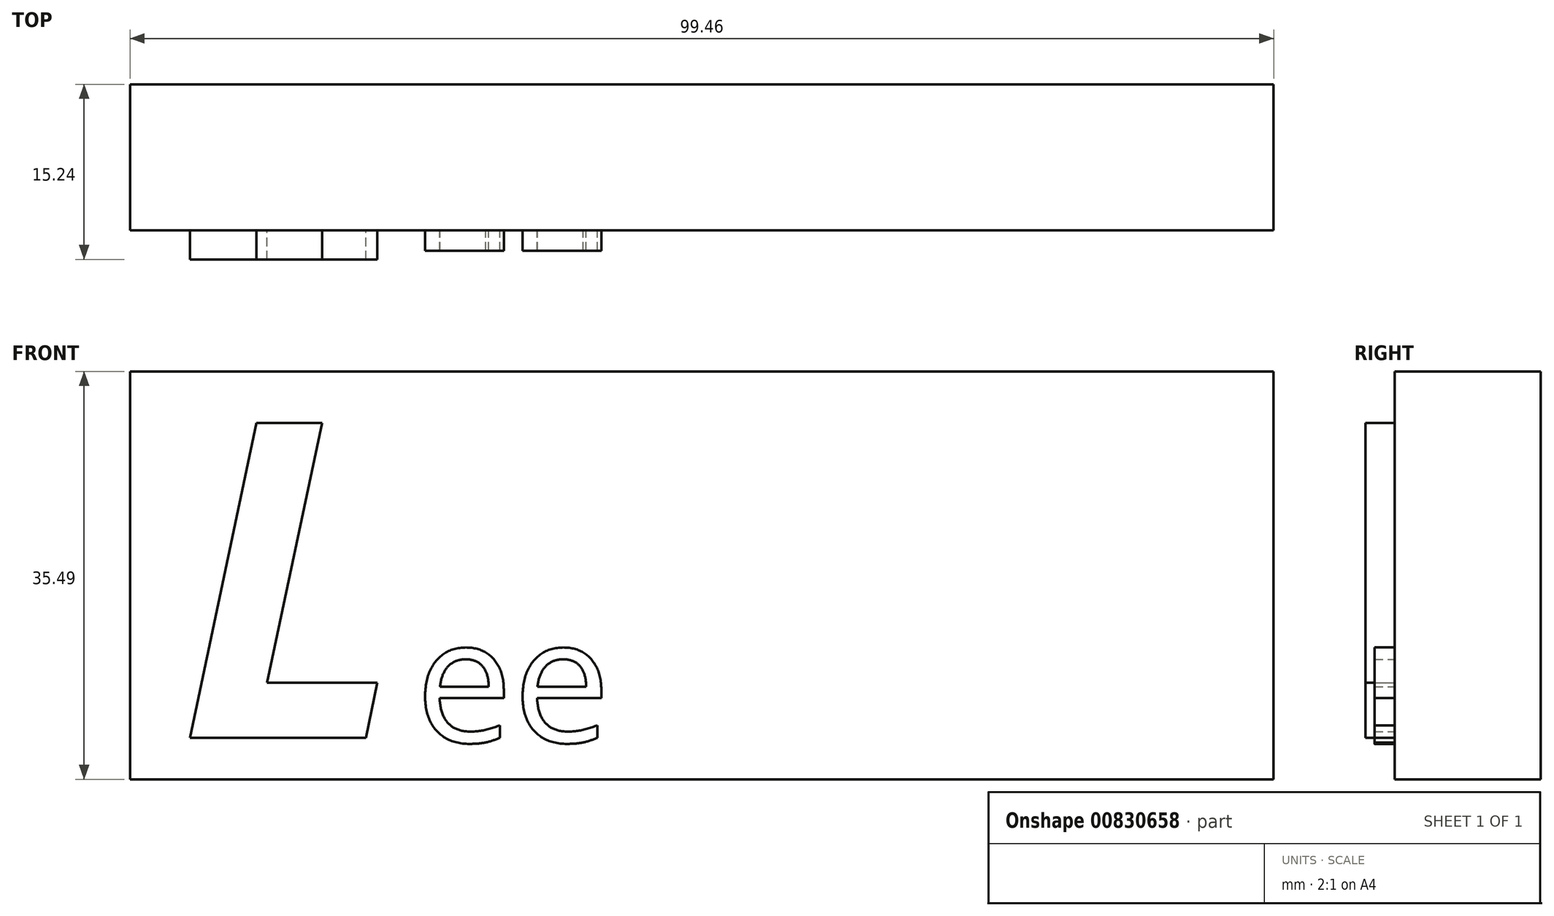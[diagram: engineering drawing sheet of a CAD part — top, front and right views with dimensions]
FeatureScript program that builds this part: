
annotation { "Feature Type Name" : "Feature", "Feature Type Description" : "" }
export const myFeature = defineFeature(function(context is Context, id is Id, definition is map)
    precondition{}
    {
        {
            var Q0;
            Q0=qCreatedBy(makeId("Front.planeOp"),FACE);
            var sketch = newSketch(context, id + "F0", { "sketchPlane" : qUnion([Q0])});
            skLineSegment(sketch, "E0.bottom", {"start": v(0, 0) * mm, "end": v(99.46, 0) * mm});
            skLineSegment(sketch, "E0.top", {"start": v(0, 35.49) * mm, "end": v(99.46, 35.49) * mm});
            skLineSegment(sketch, "E0.left", {"start": v(0, 0) * mm, "end": v(0, 35.49) * mm});
            skLineSegment(sketch, "E0.right", {"start": v(99.46, 0) * mm, "end": v(99.46, 35.49) * mm});
            skSolve(sketch);
        }
        {
            var Q0;
            Q0=makeQuery(id+"F0.imprint","IMPRINT",FACE,{"disambiguationData":[TD([[makeQuery(id+"F0.imprint","IMPRINT",EDGE,{"derivedFrom":sQuery(id+"F0.wireOp",EDGE,"E0.bottom")}),1.0]])]});
            extrude(context, id + "F1", {"entities" : qUnion([Q0]), "depth" : 12.7 * mm, "offsetDistance" : 25.4 * mm});
        }
        {
            var Q0;
            Q0=makeQuery(id+"F1.opExtrude","CAP_FACE",FACE,{"disambiguationData":[OSD([sQuery(id+"F0.wireOp",EDGE,"E0.bottom"),sQuery(id+"F0.wireOp",EDGE,"E0.top"),sQuery(id+"F0.wireOp",EDGE,"E0.left"),sQuery(id+"F0.wireOp",EDGE,"E0.right")])],"isStart":false});
            var sketch = newSketch(context, id + "F2", { "sketchPlane" : qUnion([Q0])});
            skText(sketch, "E1", { "text": "L", "fontName": "OpenSans-BoldItalic.ttf"});
            const initialGuessF2  = {"E1": [0.0042, 0.00362, 1, 0, 0.02762]};
            skSetInitialGuess(sketch, initialGuessF2);
            skSolve(sketch);
        }
        {
            var Q0;
            Q0=makeQuery(id+"F2.imprint","IMPRINT",FACE,{"disambiguationData":[TD([[makeQuery(id+"F2.imprint","IMPRINT",EDGE,{"derivedFrom":sQuery(id+"F2.wireOp",EDGE,"E1.sketch_text.stroke-0")}),-1.0]])]});
            extrude(context, id + "F3", {"entities" : qUnion([Q0]), "operationType" : NewBodyOperationType.ADD, "depth" : 2.54 * mm, "offsetDistance" : 25.4 * mm});
        }
        {
            var Q0;
            Q0=makeQuery(id+"F1.opExtrude","CAP_FACE",FACE,{"disambiguationData":[OSD([sQuery(id+"F0.wireOp",EDGE,"E0.bottom"),sQuery(id+"F0.wireOp",EDGE,"E0.top"),sQuery(id+"F0.wireOp",EDGE,"E0.left"),sQuery(id+"F0.wireOp",EDGE,"E0.right")])],"isStart":false});
            var sketch = newSketch(context, id + "F4", { "sketchPlane" : qUnion([Q0])});
            skText(sketch, "E2", { "text": "ee", "fontName": "OpenSans-Regular.ttf"});
            const initialGuessF4  = {"E2": [0.02481, 0.00323, 1, 0, 0.01088]};
            skSetInitialGuess(sketch, initialGuessF4);
            skSolve(sketch);
        }
        {
            var Q0;
            Q0 = qSketchRegion(id + "F4", true);
            extrude(context, id + "F5", {"entities" : qUnion([Q0]), "operationType" : NewBodyOperationType.ADD, "depth" : 1.78 * mm, "offsetDistance" : 25.4 * mm});
        }
    });
